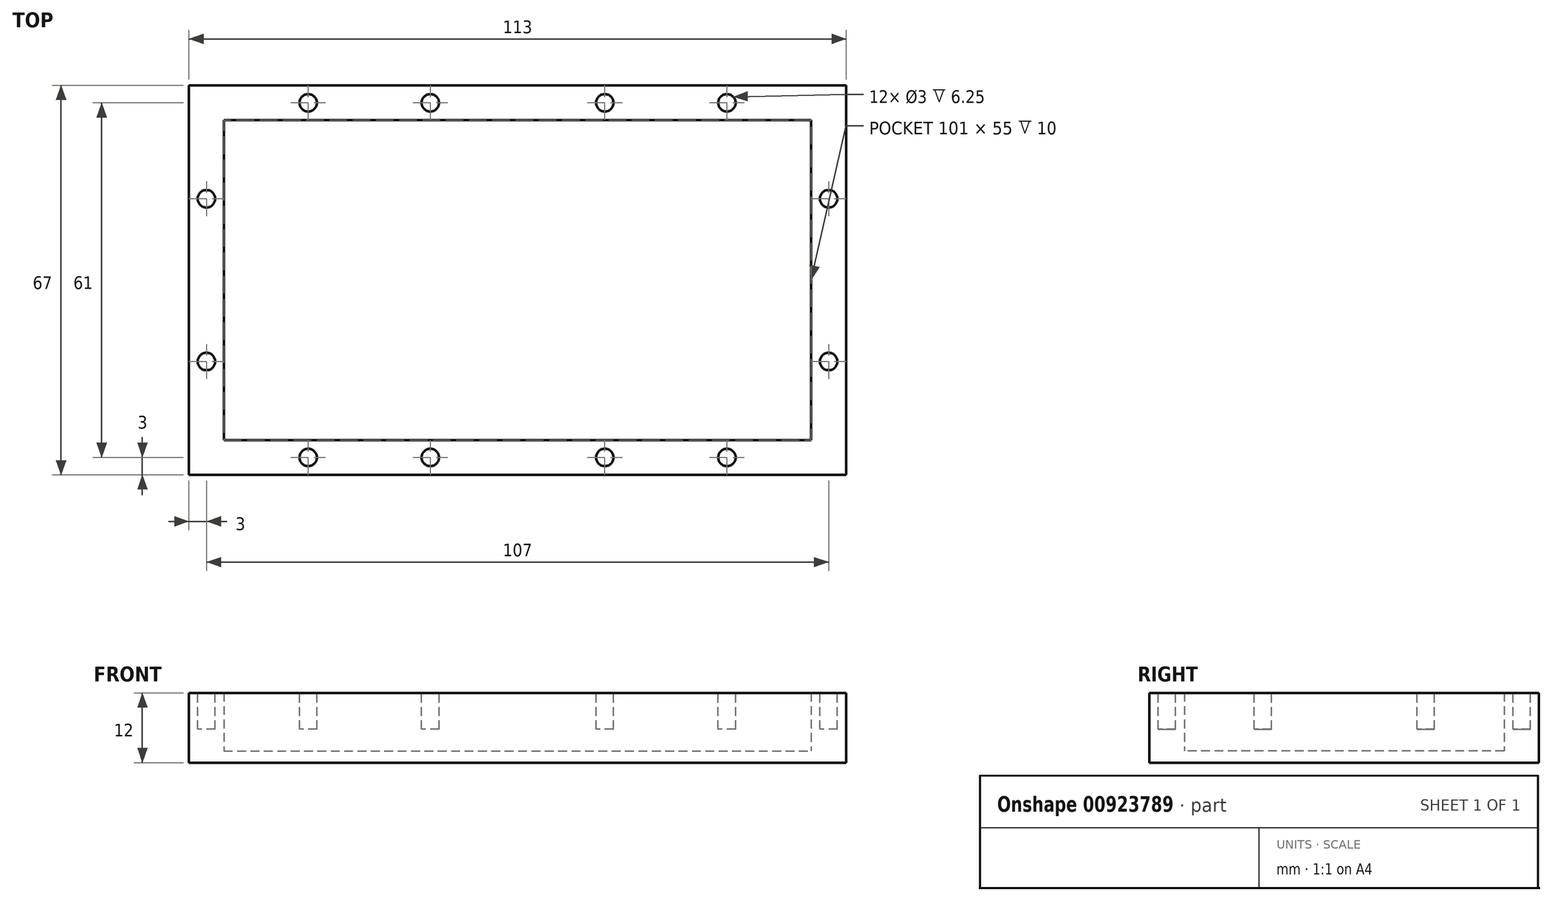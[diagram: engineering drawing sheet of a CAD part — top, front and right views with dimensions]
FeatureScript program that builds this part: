
annotation { "Feature Type Name" : "Feature", "Feature Type Description" : "" }
export const myFeature = defineFeature(function(context is Context, id is Id, definition is map)
    precondition{}
    {
        {
            var Q0;
            Q0=qCreatedBy(makeId("Top.planeOp"),FACE);
            var sketch = newSketch(context, id + "F0", { "sketchPlane" : qUnion([Q0])});
            skLineSegment(sketch, "E0.bottom", {"start": v(-56.5, 33.5) * mm, "end": v(56.5, 33.5) * mm});
            skLineSegment(sketch, "E0.top", {"start": v(-56.5, -33.5) * mm, "end": v(56.5, -33.5) * mm});
            skLineSegment(sketch, "E0.left", {"start": v(-56.5, 33.5) * mm, "end": v(-56.5, -33.5) * mm});
            skLineSegment(sketch, "E0.right", {"start": v(56.5, 33.5) * mm, "end": v(56.5, -33.5) * mm});
            skPoint(sketch, "E0.middle", {"position": v(0, 0) * mm});
            skSolve(sketch);
        }
        {
            var Q0;
            Q0 = qSketchRegion(id + "F0", true);
            extrude(context, id + "F1", {"entities" : qUnion([Q0]), "depth" : 2 * mm, "offsetDistance" : 25 * mm});
        }
        {
            var Q0;
            Q0=makeQuery(id+"F1.opExtrude","CAP_FACE",FACE,{"disambiguationData":[OSD([sQuery(id+"F0.wireOp",EDGE,"E0.bottom"),sQuery(id+"F0.wireOp",EDGE,"E0.top"),sQuery(id+"F0.wireOp",EDGE,"E0.left"),sQuery(id+"F0.wireOp",EDGE,"E0.right")])],"isStart":false});
            var sketch = newSketch(context, id + "F2", { "sketchPlane" : qUnion([Q0])});
            skLineSegment(sketch, "E1.bottom", {"start": v(-56.5, 33.5) * mm, "end": v(56.5, 33.5) * mm});
            skLineSegment(sketch, "E1.top", {"start": v(-56.5, -33.5) * mm, "end": v(56.5, -33.5) * mm});
            skLineSegment(sketch, "E1.left", {"start": v(-56.5, 33.5) * mm, "end": v(-56.5, -33.5) * mm});
            skLineSegment(sketch, "E1.right", {"start": v(56.5, 33.5) * mm, "end": v(56.5, -33.5) * mm});
            skPoint(sketch, "E1.middle", {"position": v(0, 0) * mm});
            skLineSegment(sketch, "E2.bottom", {"start": v(-50.5, 27.5) * mm, "end": v(50.5, 27.5) * mm});
            skLineSegment(sketch, "E2.top", {"start": v(-50.5, -27.5) * mm, "end": v(50.5, -27.5) * mm});
            skLineSegment(sketch, "E2.left", {"start": v(-50.5, 27.5) * mm, "end": v(-50.5, -27.5) * mm});
            skLineSegment(sketch, "E2.right", {"start": v(50.5, 27.5) * mm, "end": v(50.5, -27.5) * mm});
            skSolve(sketch);
        }
        {
            var Q0;
            Q0 = qSketchRegion(id + "F2", true);
            extrude(context, id + "F3", {"entities" : qUnion([Q0]), "operationType" : NewBodyOperationType.ADD, "depth" : 10 * mm, "offsetDistance" : 25 * mm});
        }
        {
            var Q0;
            Q0=makeQuery(id+"F3.opExtrude","CAP_FACE",FACE,{"disambiguationData":[OSD([sQuery(id+"F2.wireOp",EDGE,"E1.bottom"),sQuery(id+"F2.wireOp",EDGE,"E1.top"),sQuery(id+"F2.wireOp",EDGE,"E1.left"),sQuery(id+"F2.wireOp",EDGE,"E1.right"),sQuery(id+"F2.wireOp",EDGE,"E2.bottom"),sQuery(id+"F2.wireOp",EDGE,"E2.top"),sQuery(id+"F2.wireOp",EDGE,"E2.left"),sQuery(id+"F2.wireOp",EDGE,"E2.right")])],"isStart":false});
            var sketch = newSketch(context, id + "F4", { "sketchPlane" : qUnion([Q0])});
            skCircle(sketch, "E3", {"center": v(-36, 30.5) * mm, "radius": 1.5 * mm});
            skCircle(sketch, "E4", {"center": v(-15, 30.5) * mm, "radius": 1.5 * mm});
            skCircle(sketch, "E5.MirrorC", {"center": v(15, 30.5) * mm, "radius": 1.5 * mm});
            skCircle(sketch, "E6.MirrorC", {"center": v(36, 30.5) * mm, "radius": 1.5 * mm});
            skCircle(sketch, "E7.MirrorC", {"center": v(-15, -30.5) * mm, "radius": 1.5 * mm});
            skCircle(sketch, "E8.MirrorC", {"center": v(-36, -30.5) * mm, "radius": 1.5 * mm});
            skCircle(sketch, "E9.MirrorC", {"center": v(15, -30.5) * mm, "radius": 1.5 * mm});
            skCircle(sketch, "E10.MirrorC", {"center": v(36, -30.5) * mm, "radius": 1.5 * mm});
            skCircle(sketch, "E11", {"center": v(-53.5, 14) * mm, "radius": 1.5 * mm});
            skCircle(sketch, "E12.MirrorC", {"center": v(-53.5, -14) * mm, "radius": 1.5 * mm});
            skCircle(sketch, "E13.MirrorC", {"center": v(53.5, 14) * mm, "radius": 1.5 * mm});
            skCircle(sketch, "E14.MirrorC", {"center": v(53.5, -14) * mm, "radius": 1.5 * mm});
            skSolve(sketch);
        }
        {
            var Q0;
            Q0 = qSketchRegion(id + "F4", true);
            extrude(context, id + "F5", {"entities" : qUnion([Q0]), "operationType" : NewBodyOperationType.REMOVE, "oppositeDirection" : true, "depth" : 6.25 * mm, "offsetDistance" : 25 * mm});
        }
    });
